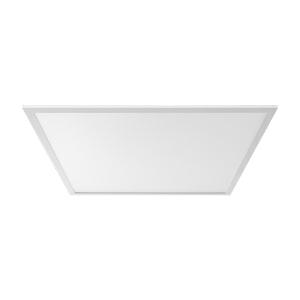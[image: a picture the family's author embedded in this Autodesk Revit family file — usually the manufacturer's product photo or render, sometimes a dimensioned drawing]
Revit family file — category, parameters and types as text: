
# Revit family: 3f_filippi_-_3f_led_panel_3f_filippi_-_22793_a01486_-_3flp6060ugr-940__1100ma____dali_68bb
name_source: partatom
category: Lighting Fixtures
units: mm (PartAtom-declared; Revit-internal decimal feet)

## family parameters
Cut with Voids When Loaded = No
Host = Face
Light Source = No
Part Type = Normal
Room Calculation Point = No
Round Connector Dimension = Use Diameter
Shared = No

## types (1)
- 3F Filippi - 3F LED Panel (1 x LED, 4436 lm, 43 W, 4000 K)
    Apparent Load = 43 VA
    Approval mark = ENEC
    CIE Flux Codes = 63 89 97 100 100
    Color Rendering = 90
    Color Temperature = 4000 K
    Control Gear = Electronic transformer
    Default Elevation = 1800 mm
    Description = ILLUMINOTECHNICAL
Luminous efficiency 100% (DLOR 100%, ULOR 0%).
Initial luminous flux of the luminaire 4436 lm.
Direct symmetric distribution.
Installation Interdistance Transv.D = 1.18 x hu - Long.D = 1.30 x hu.
Average luminance <3000 cd/m² for radial angles >65°.
Tabular UGR (CIE 117 - 4H-8H; S=0.25H; 70/50/20): RUG 18.5 - 18.7.
Beam angle: 86° - 90°.
Luminous efficacy 103 lm/W.
Lifetime (L93/B10): 30000 h. (tq+25°C)
Lifetime (L90/B10): 50000 h. (tq+25°C)
Lifetime (L80/B10): 80000 h. (tq+25°C)
Lifetime (L75/B10): 100000 h. (tq+25°C)
Sudden decreased luminous flux after 50000 hours: 0% (C0).
Photobiological safety in compliance with IEC/TR 62778: RG0 risk exempt, (IEC 62471).
In compliance with IEC/EN 62722-2-1 - IEC/EN 62717 standards.

SOURCE
2 linear LED modules 940.
Energy efficiency class (UE 2019/2020 - UE 2019/2015): C.
CIE 13.3 Colour rendering index: CRI >90 (R9 >50%).
IES TM-30 Fidelity Index: Rf = 90 Rg = 98.
CCT nominal colour temperature 4000 K.
Colour initial tolerance (MacAdam): SDCM 3.

MECHANICAL
Housing in white painted epoxy-polyester powder aluminium.
Diffuser in SMP trasparent microprismatic methacrylate (PMMA) externally, anti-glare with high transmittance.
Perimetral frame in white polycarbonate.
Anti-fall safety cable.
Luminaire with limited surface temperature. - D - (EN 60598-2-24)
Dimensions: 595x595 mm, height 9 mm. Weight 2.515 kg.
IP43 protection degree for exposed part, IP20 for recessed part.
Mechanical strength to impacts IK06 (1 joule).
Glow-wire test resistance 650°C.

ELECTRICAL
Wiring on a separate unit (Multi-current power supply, to be ordered separately).
Power of the luminaire 43 W.
CE - IEC 60598-1 - EN 60598-1.
SAFE FLICKER: PstLM=<1 and SVM=<0.4 (IEC TR 61547-1 and IEC TR 63158), to ensure a more comfortable and safe light.
Luminaire compliant with EN 60598-2-22 for power supply from a centralised emergency system CPSS (Central Power Supply System), not incorporated in the luminaire - high risk areas excluded. The default power and flux are 100% in AC and 100% in DC.
Ambient temperature from 0°C to +25°C.
Temperature class T6 max 85°C.
Relative humidity UR: <85%.

INSTALLATION
Lay-in recessed fitting / Pull-up recessed fitting with brackets / Ceiling installation with frame / Suspension via accessory.
All accessories dedicated to this product are available on the Catalog and on our website www.3F-Filippi.com.

ACCESSORIES
A01486 - DELT40C-MEL DRIVER DALI DIP-SWITCH.
DALI, PUSH-DIM, electronic wiring 230V-50/60Hz, power factor 0.95 at full load, constant output current, SELV, class II, 1 driver, 1 DALI addresse.
Multi-current power supply that allows you to choose the driving current of the fixture at the time of installation (default 900mA) according to the required illuminance.
Quick connection non-reversible plug-socket terminal block, also for cascade connection.

APPLICATIONS
Suitable product for food production plants (HACCP), IFS (Food Version 6), BRC (GSFS Food Version 7).
Environments: with VDTs, meeting rooms, offices.
Environments: recreational, transit areas, corridors, schools, stairwells.
Environments where soft diffuse light is required for optimal visual comfort.

WARNING
Luminaire designed for disposal/recycling at end-of-life.
Replaceable control gear by a professional.
    Height = 0 mm  [stored 0 ft]
    Lamp = 1 x LED
    Lamp Light Flux = 4436 lm
    Lamp Power = 43 W
    Lamp count = 1
    Length = 595 mm
    Lifetime = 50000 h
    Luminous efficacy = 103 lm/W
    Manufacturer = 3F Filippi
    ModVariant = No
    Model = 3F Filippi - 22793+A01486 - 3FLP6060UGR-940 (1100mA) + DALI
    Mounting Place = Ceiling
    Mounting Type = Recessed
    Number of Poles = 1
    OnlyDefault = Yes
    Power Factor = 1
    Product Name = 3F Filippi - 3F LED Panel
    Product group = recessed luminaire
    ProductGroupID = 4
    Protection Class = Protection class II
    Protection Degree = IP 20
    RLX_Detail_Level = 1
    RLX_Emergency_Light_Flux = 0 lm
    RLX_Emergency_Type = 0
    RLX_Emergency_Type_DB = No
    RlxData = <blob elided: 32081 chars, md5=9da5c802>
    Socket = socket
    Standby Power = 0 W
    System Light Flux = 4436 lm
    System Power = 43 W
    Type Comments = Product without accessories
    Type Image = 3ffilippi_3f_led_panel_596x596.jpg
    URL = http://relux.com
    VarID = ---
    Voltage = 0 V
    Weight = 0.00 kg
    Width = 595 mm

note: [stored X ft] marks values corroborated as IEEE doubles in the binary element streams (Revit-internal decimal feet)

## geometry (parser evidence)
native form markers: Blend x4, Sweep x10
no freeform markers — native parametric forms only
